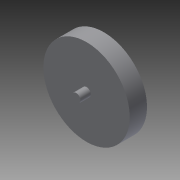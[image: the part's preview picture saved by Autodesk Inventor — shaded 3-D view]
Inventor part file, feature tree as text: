
AUTODESK INVENTOR PART (.ipt)
format: ipt  version: 2013 (Build 170138000, 138)  size: 81,920 bytes
history: native  units: mm
features: extrude x3, sketch x3, other x1
ambient origin geometry x8: Origin, YZ Plane, XZ Plane, XY Plane, X Axis, Y Axis, Z Axis, Center Point
feature tree (7):
  other  "ソリッド1"
  extrude  "押し出し1"  Depth=25.0mm
  extrude  "押し出し2"  Depth=5.0mm TaperAngle=0.0deg
  extrude  "押し出し3"  Depth=2.5mm
  sketch  "スケッチ1"
  sketch  "スケッチ2"
  sketch  "スケッチ3"
